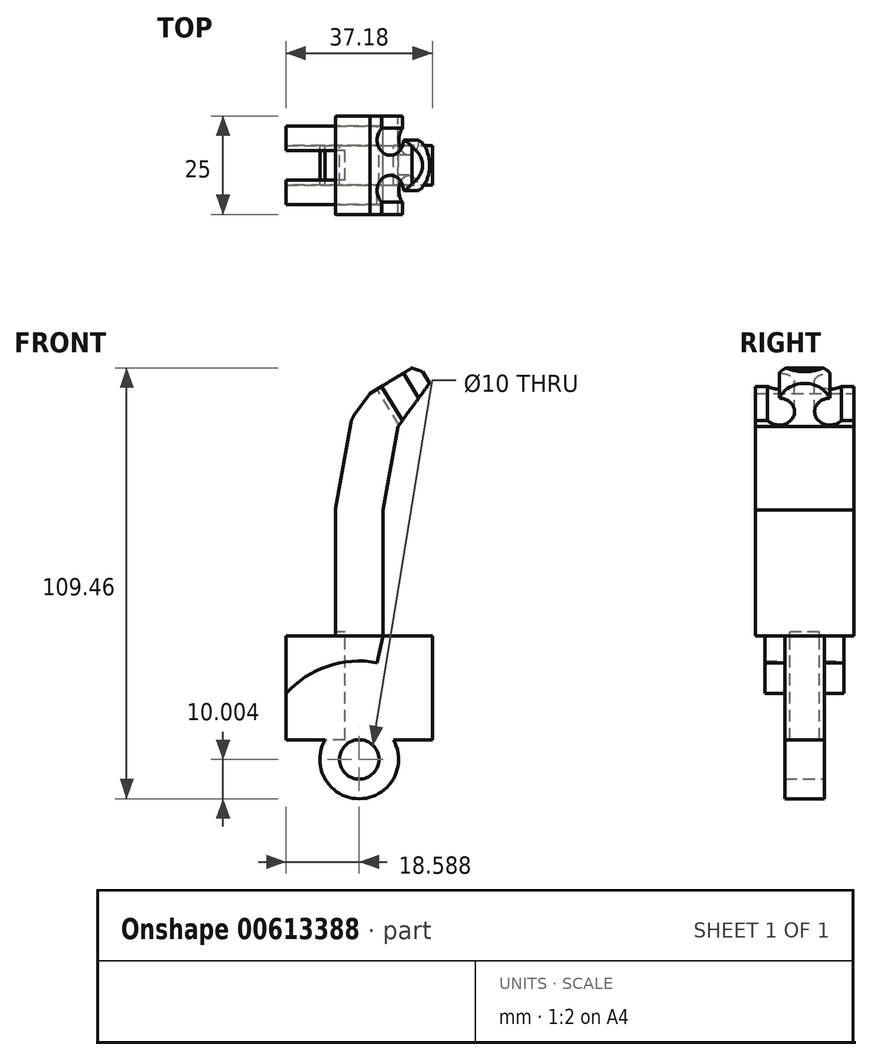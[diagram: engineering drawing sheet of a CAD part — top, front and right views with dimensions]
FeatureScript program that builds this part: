
annotation { "Feature Type Name" : "Feature", "Feature Type Description" : "" }
export const myFeature = defineFeature(function(context is Context, id is Id, definition is map)
    precondition{}
    {
        {
            var Q0;
            Q0=qCreatedBy(makeId("Front.planeOp"),FACE);
            var sketch = newSketch(context, id + "F0", { "sketchPlane" : qUnion([Q0])});
            skLineSegment(sketch, "E0.bottom", {"start": v(-21.16, -53.13) * mm, "end": v(-19.9, -53.13) * mm});
            skLineSegment(sketch, "E0.left", {"start": v(-21.16, -53.13) * mm, "end": v(-21.16, -26.7) * mm});
            skLineSegment(sketch, "E0.right", {"start": v(16.02, -53.13) * mm, "end": v(16.02, -26.7) * mm});
            skPoint(sketch, "E1.centerSnap0", {"position": v(-2.57, -53.13) * mm});
            skPoint(sketch, "E2.centerSnap0", {"position": v(-2.57, 46.87) * mm});
            skLineSegment(sketch, "E3.trimOffspring", {"start": v(14.75, -53.13) * mm, "end": v(16.02, -53.13) * mm});
            skCircle(sketch, "E4", {"center": v(-2.57, -58.13) * mm, "radius": 5 * mm});
            skArc(sketch, "E5", {"start": v(16.02, -41.41) * mm, "mid": v(-2.57, -33.13) * mm, "end": v(-21.16, -41.41) * mm});
            skArc(sketch, "E6", {"start": v(-11.23, -53.13) * mm, "mid": v(-2.57, -68.13) * mm, "end": v(6.09, -53.13) * mm});
            skLineSegment(sketch, "E7", {"start": v(14.75, -53.13) * mm, "end": v(6.09, -53.13) * mm});
            skLineSegment(sketch, "E8", {"start": v(-21.16, -26.7) * mm, "end": v(16.02, -26.7) * mm});
            skPoint(sketch, "E2.center.orphan", {"position": v(-2.57, 56.87) * mm});
            skPoint(sketch, "E0.top.start.orphan", {"position": v(-21.16, 46.87) * mm});
            skPoint(sketch, "E9.trimOffspring.end.orphan", {"position": v(16.02, 46.87) * mm});
            skLineSegment(sketch, "E10.bottom", {"start": v(-8.6, -26.7) * mm, "end": v(3.47, -26.7) * mm});
            skLineSegment(sketch, "E10.top", {"start": v(-8.6, 5.2) * mm, "end": v(3.47, 5.2) * mm});
            skLineSegment(sketch, "E10.left", {"start": v(-8.6, -26.7) * mm, "end": v(-8.6, 5.2) * mm});
            skLineSegment(sketch, "E10.right", {"start": v(3.47, -26.7) * mm, "end": v(3.47, 5.2) * mm});
            skLineSegment(sketch, "E11", {"start": v(-8.6, 5.2) * mm, "end": v(-4.45, 28.57) * mm});
            skLineSegment(sketch, "E12", {"start": v(-4.45, 28.57) * mm, "end": v(7.25, 26.48) * mm});
            skLineSegment(sketch, "E13", {"start": v(7.25, 26.48) * mm, "end": v(3.47, 5.2) * mm});
            skLineSegment(sketch, "E14", {"start": v(-4.45, 28.57) * mm, "end": v(6.11, 42.97) * mm});
            skLineSegment(sketch, "E15", {"start": v(6.11, 42.97) * mm, "end": v(16.67, 39.32) * mm});
            skLineSegment(sketch, "E16", {"start": v(16.67, 39.32) * mm, "end": v(7.25, 26.48) * mm});
            skPoint(sketch, "E17", {"position": v(-2.57, -26.7) * mm});
            skLineSegment(sketch, "E18.trimOffspring", {"start": v(-11.23, -53.13) * mm, "end": v(-19.9, -53.13) * mm});
            skLineSegment(sketch, "E19", {"start": v(3.47, -26.7) * mm, "end": v(1.98, -33.54) * mm});
            skSolve(sketch);
        }
        {
            var Q0;
            {var subQ6=sQuery(id+"F0.wireOp",EDGE,"E19");Q0=makeQuery(id+"F0.imprint","IMPRINT",FACE,{"disambiguationData":[TD([[makeQuery(id+"F0.imprint","IMPRINT",EDGE,{"derivedFrom":subQ6}),-1.0]])]});}
            extrude(context, id + "F1", {"entities" : qUnion([Q0]), "endBound" : BoundingType.SYMMETRIC, "depth" : 20 * mm, "offsetDistance" : 25 * mm});
        }
        {
            var Q0;
            {var subQ5=sQuery(id+"F0.wireOp",EDGE,"E0.bottom");Q0=makeQuery(id+"F0.imprint","IMPRINT",FACE,{"disambiguationData":[TD([[makeQuery(id+"F0.imprint","IMPRINT",EDGE,{"derivedFrom":subQ5}),1.0]])]});}
            var Q1;
            {var subQ5=sQuery(id+"F0.wireOp",EDGE,"E19");Q1=makeQuery(id+"F0.imprint","IMPRINT",FACE,{"disambiguationData":[TD([[makeQuery(id+"F0.imprint","IMPRINT",EDGE,{"derivedFrom":subQ5}),1.0]])]});}
            extrude(context, id + "F2", {"entities" : qUnion([Q0, Q1]), "operationType" : NewBodyOperationType.ADD, "endBound" : BoundingType.SYMMETRIC, "depth" : 10 * mm, "offsetDistance" : 25 * mm});
        }
        {
            var Q0;
            Q0=makeQuery(id+"F0.imprint","IMPRINT",FACE,{"disambiguationData":[TD([[makeQuery(id+"F0.imprint","IMPRINT",EDGE,{"derivedFrom":sQuery(id+"F0.wireOp",EDGE,"E10.top")}),-1.0]])]});
            var Q1;
            Q1=makeQuery(id+"F0.imprint","IMPRINT",FACE,{"disambiguationData":[TD([[makeQuery(id+"F0.imprint","IMPRINT",EDGE,{"derivedFrom":sQuery(id+"F0.wireOp",EDGE,"E10.top")}),1.0]])]});
            var Q2;
            Q2=makeQuery(id+"F0.imprint","IMPRINT",FACE,{"disambiguationData":[TD([[makeQuery(id+"F0.imprint","IMPRINT",EDGE,{"derivedFrom":sQuery(id+"F0.wireOp",EDGE,"E12")}),1.0]])]});
            extrude(context, id + "F3", {"entities" : qUnion([Q0, Q1, Q2]), "operationType" : NewBodyOperationType.ADD, "endBound" : BoundingType.SYMMETRIC, "depth" : 25 * mm, "offsetDistance" : 25 * mm});
        }
        {
            var Q0;
            Q0=makeQuery(id+"F3.opExtrude","SWEPT_EDGE",EDGE,{"disambiguationData":[OSD([sQuery(id+"F0.wireOp",EDGE,"E10.top"),sQuery(id+"F0.wireOp",EDGE,"E10.left"),sQuery(id+"F0.wireOp",EDGE,"E11")])]});
            var Q1;
            Q1=makeQuery(id+"F3.opExtrude","SWEPT_EDGE",EDGE,{"disambiguationData":[OSD([sQuery(id+"F0.wireOp",EDGE,"E11"),sQuery(id+"F0.wireOp",EDGE,"E12"),sQuery(id+"F0.wireOp",EDGE,"E14")])]});
            fillet(context, id + "F4", {"entities" : qUnion([Q0, Q1]), "radius" : 5 * mm, "tangentPropagation" : true, "allowEdgeOverflow" : false});
        }
        {
            var Q0;
            Q0=makeQuery(id+"F3.opExtrude","SWEPT_EDGE",EDGE,{"disambiguationData":[OSD([sQuery(id+"F0.wireOp",EDGE,"E14"),sQuery(id+"F0.wireOp",EDGE,"E15")])]});
            chamfer(context, id + "F5", {"entities" : qUnion([Q0]), "chamferType" : ChamferType.TWO_OFFSETS, "width1" : 10 * mm, "oppositeDirection" : false, "width2" : 5 * mm, "tangentPropagation" : true});
        }
        {
            var Q0;
            Q0=makeQuery(id+"F5.opChamfer","BLEND_FACE",FACE,{"disambiguationData":[OSD([sQuery(id+"F0.wireOp",EDGE,"E14"),sQuery(id+"F0.wireOp",EDGE,"E15")])]});
            var sketch = newSketch(context, id + "F6", { "sketchPlane" : qUnion([Q0])});
            skArc(sketch, "E20", {"start": v(21.66, 9.4) * mm, "mid": v(22.6, 2.9) * mm, "end": v(28.12, 6.45) * mm});
            skArc(sketch, "E21", {"start": v(28.12, -6.45) * mm, "mid": v(22.6, -2.9) * mm, "end": v(21.66, -9.4) * mm});
            skLineSegment(sketch, "E22", {"start": v(18.23, 12.5) * mm, "end": v(18.23, -12.5) * mm});
            skLineSegment(sketch, "E23", {"start": v(18.23, -12.5) * mm, "end": v(21.66, -12.5) * mm});
            skLineSegment(sketch, "E24", {"start": v(21.66, -12.5) * mm, "end": v(21.66, -9.4) * mm});
            skLineSegment(sketch, "E25", {"start": v(18.23, 12.5) * mm, "end": v(21.66, 12.5) * mm});
            skLineSegment(sketch, "E26", {"start": v(21.66, 12.5) * mm, "end": v(21.66, 9.4) * mm});
            skPoint(sketch, "E27", {"position": v(28.12, 6.45) * mm});
            skPoint(sketch, "E28", {"position": v(28.12, -6.45) * mm});
            skArc(sketch, "E29", {"start": v(28.12, -6.45) * mm, "mid": v(32.48, 0) * mm, "end": v(28.12, 6.45) * mm});
            skLineSegment(sketch, "E30", {"start": v(21.66, 12.5) * mm, "end": v(39.18, 12.5) * mm});
            skLineSegment(sketch, "E31", {"start": v(39.18, 12.5) * mm, "end": v(39.18, -12.5) * mm});
            skLineSegment(sketch, "E32", {"start": v(39.18, -12.5) * mm, "end": v(21.66, -12.5) * mm});
            skSolve(sketch);
        }
        {
            var Q0;
            {var subQ0=sQuery(id+"F6.wireOp",EDGE,"E31");Q0=makeQuery(id+"F6.imprint","IMPRINT",FACE,{"disambiguationData":[TD([[makeQuery(id+"F6.imprint","IMPRINT",EDGE,{"derivedFrom":subQ0}),-1.0]])]});}
            var Q1;
            {var subQ1=sQuery(id+"F6.wireOp",EDGE,"E20");Q1=makeQuery(id+"F6.imprint","IMPRINT",FACE,{"disambiguationData":[TD([[makeQuery(id+"F6.imprint","IMPRINT",EDGE,{"derivedFrom":subQ1}),1.0]])]});}
            var Q2;
            {var subQ1=sQuery(id+"F6.wireOp",EDGE,"E21");Q2=makeQuery(id+"F6.imprint","IMPRINT",FACE,{"disambiguationData":[TD([[makeQuery(id+"F6.imprint","IMPRINT",EDGE,{"derivedFrom":subQ1}),1.0]])]});}
            extrude(context, id + "F7", {"entities" : qUnion([Q0, Q1, Q2]), "operationType" : NewBodyOperationType.REMOVE, "oppositeDirection" : true, "depth" : 25 * mm, "offsetDistance" : 25 * mm});
        }
        {
            var Q0;
            {var subQ0=sQuery(id+"F0.wireOp",EDGE,"E0.left");Q0=makeQuery(id+"F2.boolean.opBoolean","MERGE",FACE,{"derivedFrom":[makeQuery(id+"F1.opExtrude","SWEPT_FACE",FACE,{"disambiguationData":[OSD([subQ0])]}),makeQuery(id+"F2.opExtrude","SWEPT_FACE",FACE,{"disambiguationData":[OSD([subQ0])]})]});}
            var sketch = newSketch(context, id + "F8", { "sketchPlane" : qUnion([Q0])});
            skLineSegment(sketch, "E33.bottom", {"start": v(-3.75, -53.13) * mm, "end": v(3.75, -53.13) * mm});
            skLineSegment(sketch, "E33.top", {"start": v(-3.75, -25.7) * mm, "end": v(3.75, -25.7) * mm});
            skLineSegment(sketch, "E33.left", {"start": v(-3.75, -53.13) * mm, "end": v(-3.75, -25.7) * mm});
            skLineSegment(sketch, "E33.right", {"start": v(3.75, -53.13) * mm, "end": v(3.75, -25.7) * mm});
            skSolve(sketch);
        }
        {
            var Q0;
            Q0 = qSketchRegion(id + "F8", true);
            extrude(context, id + "F9", {"entities" : qUnion([Q0]), "operationType" : NewBodyOperationType.REMOVE, "oppositeDirection" : true, "depth" : 15 * mm, "offsetDistance" : 25 * mm});
        }
    });
